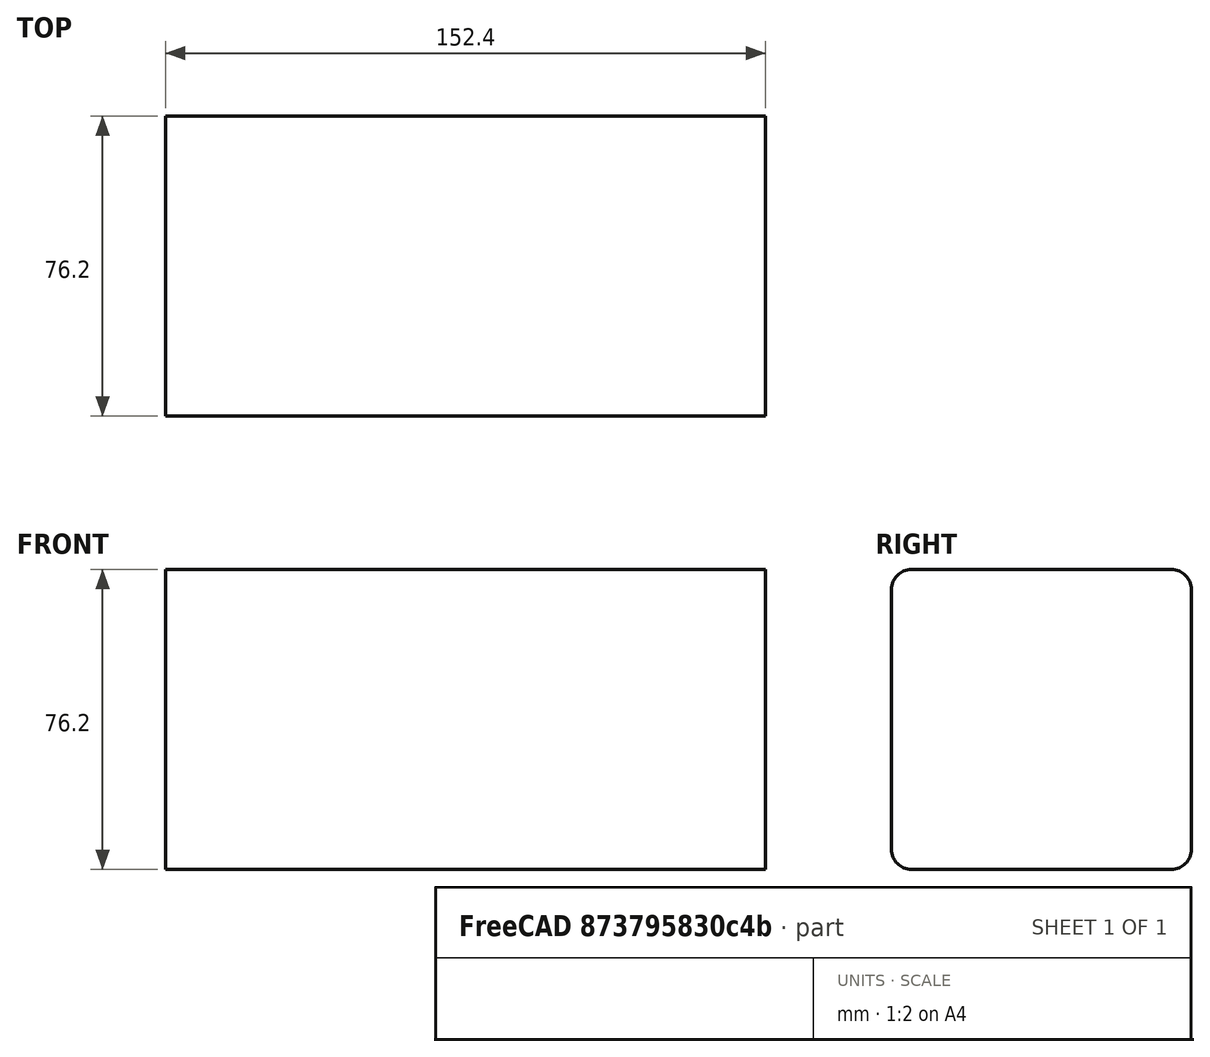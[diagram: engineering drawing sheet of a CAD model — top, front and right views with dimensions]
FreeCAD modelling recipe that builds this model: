
FCSTD DOCUMENT  (FreeCAD 0.20RUnknown)
Label: frame-76.2mmx2
License: All rights reserved
LicenseURL: http://en.wikipedia.org/wiki/All_rights_reserved
objects: PartDesign::Fillet×4, PartDesign::AdditiveBox×1, PartDesign::Body×1
note: 11 computed .brp shape members not serialized (recipe doc carries the construction recipe); baked Part::Feature solids carry a one-line shape summary decoded from their .brp

FEATURE [PartDesign::AdditiveBox] Box
  AttacherType = Attacher::AttachEngine3D
  Height = 76.2
  Length = 152.4
  Width = 76.2
FEATURE [PartDesign::Fillet] Fillet
  Base = -> Box [Edge10]
  BaseFeature = -> Box
  Radius = 5.08
  SupportTransform = false
  UseAllEdges = false
FEATURE [PartDesign::Fillet] Fillet001
  Base = -> Fillet [Edge13]
  BaseFeature = -> Fillet
  Radius = 5.08
  SupportTransform = false
  UseAllEdges = false
FEATURE [PartDesign::Fillet] Fillet002
  Base = -> Fillet001 [Edge15]
  BaseFeature = -> Fillet001
  Radius = 5.08
  SupportTransform = false
  UseAllEdges = false
FEATURE [PartDesign::Fillet] Fillet003
  Base = -> Fillet002 [Edge15]
  BaseFeature = -> Fillet002
  Radius = 5.08
  SupportTransform = false
  UseAllEdges = false
FEATURE [PartDesign::Body] Body
  Group = -> [Box,Fillet,Fillet001,Fillet002,Fillet003]
  Origin = -> Origin
  Tip = -> Fillet003
